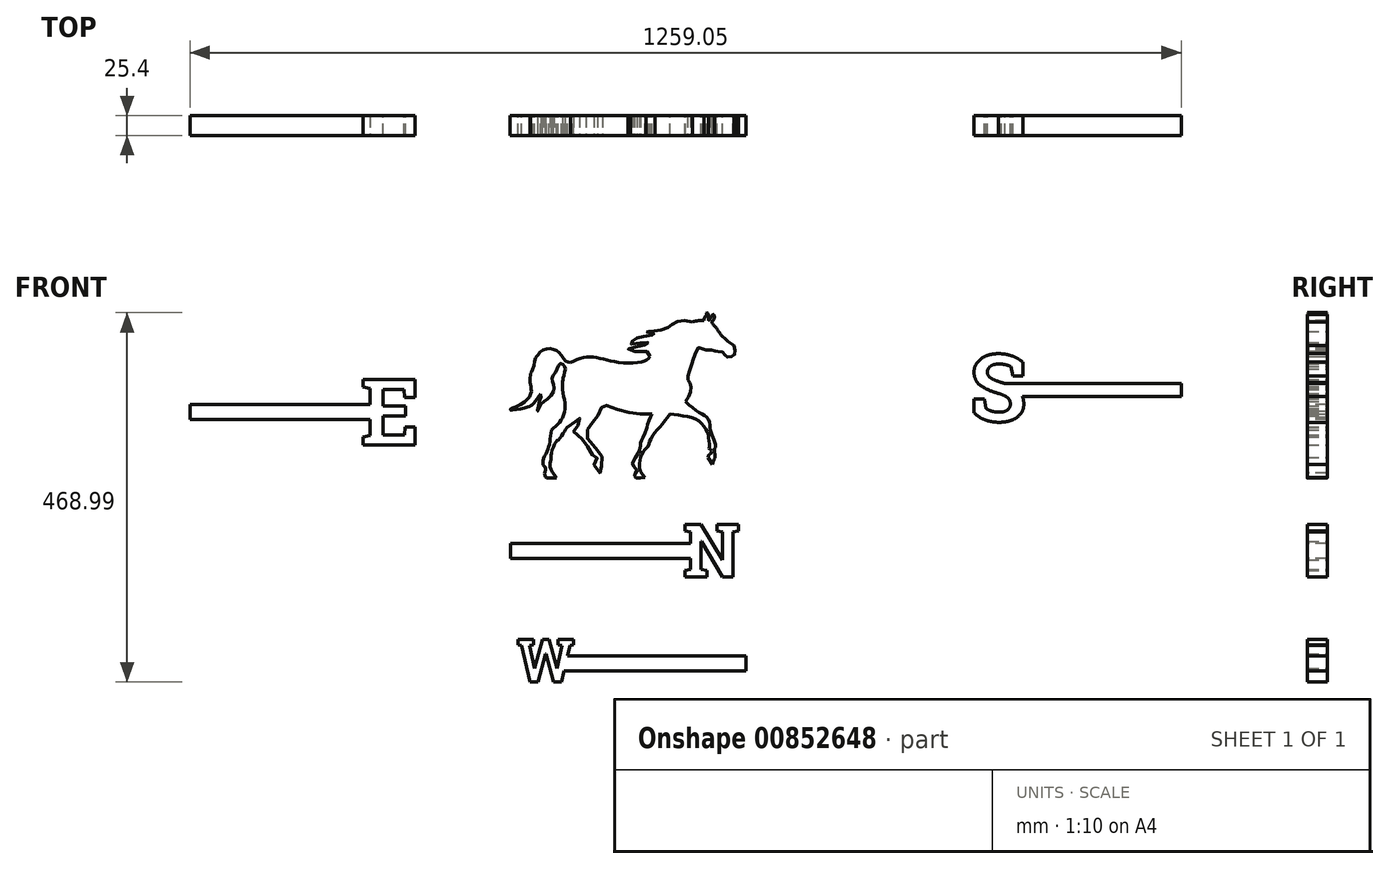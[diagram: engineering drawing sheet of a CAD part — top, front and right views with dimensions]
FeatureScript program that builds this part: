
annotation { "Feature Type Name" : "Feature", "Feature Type Description" : "" }
export const myFeature = defineFeature(function(context is Context, id is Id, definition is map)
    precondition{}
    {
        {
            var Q0;
            Q0=qCreatedBy(makeId("Front.planeOp"),FACE);
            var sketch = newSketch(context, id + "F0", { "sketchPlane" : qUnion([Q0])});
            skFitSpline(sketch, "E0", {"points": [v(155.5, 210.54) * mm, v(173.74, 216.9) * mm, v(192.53, 215.79) * mm, v(216.57, 210.54) * mm, v(248.62, 211.92) * mm, v(256.36, 217.72) * mm, v(273.76, 237.07) * mm, v(292.55, 252.27) * mm, v(310.24, 261.94) * mm, v(324.6, 263.88) * mm], "startDerivative": vector(167.31, 74.76) * mm, "endDerivative": vector(151.86, 5.73) * mm});
            skFitSpline(sketch, "E1", {"points": [v(324.6, 263.88) * mm, v(326.8, 269.35) * mm, v(327.97, 270.63) * mm, v(328.55, 273.53) * mm, v(330.64, 270.86) * mm, v(330.87, 263.88) * mm, v(336.68, 271.32) * mm, v(337.5, 265.17) * mm, v(334.7, 261.8) * mm, v(339.35, 255.52) * mm, v(347.49, 244.48) * mm, v(362.7, 232.05) * mm], "startDerivative": vector(24.18, 79.73) * mm, "endDerivative": vector(109.46, -77.63) * mm});
            skLineSegment(sketch, "E2", {"start": v(334.7, 261.8) * mm, "end": v(336.68, 271.32) * mm});
            skFitSpline(sketch, "E3", {"points": [v(362.7, 232.05) * mm, v(364.22, 221.36) * mm, v(359.57, 217.87) * mm, v(352.37, 218) * mm, v(349.23, 223.34) * mm, v(340.52, 224.38) * mm, v(336.91, 226) * mm, v(325.53, 226.7) * mm, v(318.2, 229.5) * mm, v(312.28, 217.18) * mm, v(306.02, 198.3) * mm, v(304.27, 188.92) * mm, v(307.59, 182.66) * mm, v(307.69, 172.9) * mm, v(301.34, 160.58) * mm], "startDerivative": vector(46.46, -160.08) * mm, "endDerivative": vector(-88.77, -140.52) * mm});
            skFitSpline(sketch, "E4", {"points": [v(301.34, 160.58) * mm, v(316.39, 148.52) * mm, v(324.98, 143.15) * mm, v(330.06, 138.75) * mm, v(332.6, 130.93) * mm, v(333.1, 123.31) * mm, v(339.54, 103.38) * mm, v(337.98, 100.45) * mm, v(339.05, 90.97) * mm, v(337.2, 86.87) * mm, v(335.53, 80.8) * mm], "startDerivative": vector(107.76, -91.14) * mm, "endDerivative": vector(-14.64, -79.86) * mm});
            skLineSegment(sketch, "E5", {"start": v(335.53, 80.8) * mm, "end": v(330.06, 89.4) * mm});
            skFitSpline(sketch, "E6", {"points": [v(330.06, 89.4) * mm, v(330.75, 92.92) * mm, v(333.58, 94.3) * mm, v(334.07, 99.67) * mm, v(331.33, 100.74) * mm, v(331.72, 104.36) * mm, v(330.94, 112.56) * mm, v(330.06, 120.67) * mm, v(324.88, 129.08) * mm, v(315.6, 137.77) * mm, v(298.8, 142.46) * mm, v(281.7, 144.9) * mm], "startDerivative": vector(-0.67, 69.7) * mm, "endDerivative": vector(-122.74, 16.45) * mm});
            skFitSpline(sketch, "E7", {"points": [v(281.7, 144.9) * mm, v(271.15, 130.93) * mm, v(260.4, 118.65) * mm, v(255.72, 109.08) * mm, v(253.57, 103.38) * mm, v(249.47, 99.67) * mm, v(244.97, 91.1) * mm, v(243.21, 82.5) * mm, v(243.07, 75.41) * mm, v(250.13, 64.4) * mm], "startDerivative": vector(-68.9, -98.06) * mm, "endDerivative": vector(72.71, -90.96) * mm});
            skFitSpline(sketch, "E8", {"points": [v(250.13, 64.4) * mm, v(237.69, 64.4) * mm, v(237.2, 69.26) * mm, v(239.54, 73.56) * mm, v(235.64, 78.54) * mm, v(234.27, 82.5) * mm, v(238.47, 90.95) * mm, v(243.94, 101.6) * mm, v(244.43, 109.32) * mm, v(246.87, 114.5) * mm, v(251.82, 126.23) * mm, v(252.23, 127.8) * mm, v(254.86, 136.42) * mm, v(258.72, 144.9) * mm], "startDerivative": vector(-155.51, -25.86) * mm, "endDerivative": vector(45.7, 89.67) * mm});
            skFitSpline(sketch, "E9", {"points": [v(258.72, 144.9) * mm, v(241.65, 144.9) * mm, v(223.83, 148.08) * mm, v(206.42, 153.75) * mm, v(196.33, 156.51) * mm, v(194.12, 150.3) * mm, v(189.43, 141.86) * mm, v(182.93, 133.85) * mm, v(177.27, 125.97) * mm, v(175.75, 115.75) * mm, v(188.73, 100.27) * mm, v(195.5, 89.08) * mm, v(194.68, 77.47) * mm, v(193.16, 70.01) * mm, v(185.28, 79.4) * mm, v(187.35, 84.1) * mm, v(189.01, 91.3) * mm, v(183.48, 92.81) * mm, v(177, 103.31) * mm, v(169.8, 113.12) * mm, v(159.17, 123.63) * mm, v(163.73, 129.43) * mm, v(166.77, 135.1) * mm, v(166.21, 140.62) * mm, v(162.48, 136.34) * mm, v(150.74, 128.05) * mm], "startDerivative": vector(-332.87, -13.48) * mm, "endDerivative": vector(-283.34, -157.92) * mm});
            skFitSpline(sketch, "E10", {"points": [v(150.74, 128.05) * mm, v(145.93, 120.3) * mm, v(139.98, 112.16) * mm, v(136.67, 109.53) * mm, v(131.42, 96.54) * mm, v(130.59, 88.53) * mm, v(129.48, 83.14) * mm, v(129.62, 76.92) * mm, v(137.36, 63.52) * mm], "startDerivative": vector(-35.37, -57.03) * mm, "endDerivative": vector(59.69, -86.9) * mm});
            skLineSegment(sketch, "E11", {"start": v(137.36, 63.52) * mm, "end": v(125.06, 63.52) * mm});
            skFitSpline(sketch, "E12", {"points": [v(125.06, 63.52) * mm, v(122.58, 67.8) * mm, v(123.27, 73.33) * mm, v(123, 77.61) * mm, v(120.78, 80.24) * mm, v(121.06, 87.84) * mm, v(126.03, 98.48) * mm, v(128.93, 109.4) * mm, v(131.28, 124.73) * mm], "startDerivative": vector(-32.82, 39.9) * mm, "endDerivative": vector(12.86, 89.42) * mm});
            skFitSpline(sketch, "E13", {"points": [v(131.28, 124.73) * mm, v(139.5, 132.14) * mm, v(145.95, 141.9) * mm, v(148.49, 155.59) * mm, v(145.75, 172.2) * mm, v(144.97, 185.88) * mm, v(145.75, 189.2) * mm, v(149.27, 201.9) * mm, v(155.5, 210.54) * mm], "startDerivative": vector(69.41, 57.06) * mm, "endDerivative": vector(57.1, 60.66) * mm});
            skFitSpline(sketch, "E14", {"points": [v(149.27, 201.9) * mm, v(146.66, 207.13) * mm, v(142.12, 209) * mm, v(137.72, 200.47) * mm, v(132.52, 192.2) * mm, v(132.52, 185.26) * mm, v(134.52, 176.46) * mm, v(125.72, 163.65) * mm, v(116.65, 155.52) * mm, v(113.31, 148.05) * mm, v(116.11, 161.65) * mm, v(116.91, 170.06) * mm, v(104.91, 180.06) * mm, v(104.38, 194.2) * mm, v(104.38, 196.46) * mm, v(107.45, 201.9) * mm, v(110.91, 216.07) * mm, v(113.18, 219) * mm, v(120.38, 226.34) * mm, v(132.92, 227.27) * mm, v(141.19, 222.47) * mm, v(149.27, 212.07) * mm, v(155.5, 210.54) * mm], "startDerivative": vector(-73.14, 221) * mm, "endDerivative": vector(242.16, -2.9) * mm});
            skFitSpline(sketch, "E15.trimOffspring", {"points": [v(149.27, 201.9) * mm, v(146.66, 207.13) * mm, v(142.12, 209) * mm, v(137.72, 200.47) * mm, v(132.52, 192.2) * mm, v(132.52, 185.26) * mm, v(134.52, 176.46) * mm, v(125.72, 163.65) * mm, v(116.65, 155.52) * mm, v(113.31, 148.05) * mm, v(116.11, 161.65) * mm, v(116.91, 170.06) * mm, v(104.91, 180.06) * mm, v(104.38, 194.2) * mm, v(104.38, 196.46) * mm, v(107.45, 201.9) * mm, v(110.91, 216.07) * mm, v(113.18, 219) * mm, v(120.38, 226.34) * mm, v(132.92, 227.27) * mm, v(141.19, 222.47) * mm, v(149.27, 212.07) * mm, v(155.5, 210.54) * mm], "startDerivative": vector(-73.14, 221) * mm, "endDerivative": vector(242.16, -2.9) * mm});
            skFitSpline(sketch, "E16", {"points": [v(104.91, 180.06) * mm, v(104.91, 170.72) * mm, v(91.78, 156.72) * mm, v(78.45, 150.31) * mm, v(94.05, 151.65) * mm, v(104.91, 155.38) * mm, v(106.86, 156.72) * mm, v(116.91, 170.06) * mm], "startDerivative": vector(12.52, -71.7) * mm, "endDerivative": vector(72.4, 101.25) * mm});
            skFitSpline(sketch, "E17", {"points": [v(310.24, 261.94) * mm, v(296.7, 263.59) * mm, v(286.52, 260.38) * mm, v(282, 256.8) * mm, v(274.26, 252.84) * mm, v(261.81, 250.2) * mm, v(257.85, 249.82) * mm, v(251.44, 249.82) * mm, v(256.53, 247.74) * mm, v(262.56, 246.42) * mm, v(252.2, 244.16) * mm, v(240.68, 241.9) * mm, v(234.84, 238.31) * mm, v(231.44, 234.16) * mm, v(244.08, 235.1) * mm, v(253.89, 235.67) * mm, v(242, 230.58) * mm, v(228.61, 227.75) * mm, v(237.67, 224.16) * mm, v(240.68, 224.16) * mm, v(252.38, 224.35) * mm, v(256.36, 217.72) * mm], "startDerivative": vector(-229.47, 50.05) * mm, "endDerivative": vector(46.47, -183.94) * mm});
            skSolve(sketch);
        }
        {
            var Q0;
            Q0 = qSketchRegion(id + "F0", true);
            extrude(context, id + "F1", {"entities" : qUnion([Q0]), "depth" : 25.4 * mm, "offsetDistance" : 25.4 * mm});
        }
        {
            var Q0;
            Q0 = qSketchRegion(id + "F0", true);
            extrude(context, id + "F2", {"entities" : qUnion([Q0]), "operationType" : NewBodyOperationType.ADD, "depth" : 25.4 * mm, "offsetDistance" : 25.4 * mm});
        }
        {
            var Q0;
            Q0=qCreatedBy(makeId("Front.planeOp"),FACE);
            var sketch = newSketch(context, id + "F3", { "sketchPlane" : qUnion([Q0])});
            skText(sketch, "E18", { "text": "N", "fontName": "RobotoSlab-Bold.ttf"});
            const initialGuessF3  = {"E18": [0.29832, -0.06195, 1, 0, 0.0673]};
            skSetInitialGuess(sketch, initialGuessF3);
            skSolve(sketch);
        }
        {
            var Q0;
            Q0 = qSketchRegion(id + "F3", true);
            extrude(context, id + "F4", {"entities" : qUnion([Q0]), "depth" : 25.4 * mm, "offsetDistance" : 25.4 * mm});
        }
        {
            var Q0;
            Q0=makeQuery(id+"F4.opExtrude","CAP_FACE",FACE,{"disambiguationData":[OSD([sQuery(id+"F3.wireOp",EDGE,"E18.sketch_text.stroke-0"),sQuery(id+"F3.wireOp",EDGE,"E18.sketch_text.stroke-1"),sQuery(id+"F3.wireOp",EDGE,"E18.sketch_text.stroke-2"),sQuery(id+"F3.wireOp",EDGE,"E18.sketch_text.stroke-3"),sQuery(id+"F3.wireOp",EDGE,"E18.sketch_text.stroke-4"),sQuery(id+"F3.wireOp",EDGE,"E18.sketch_text.stroke-5"),sQuery(id+"F3.wireOp",EDGE,"E18.sketch_text.stroke-6"),sQuery(id+"F3.wireOp",EDGE,"E18.sketch_text.stroke-7"),sQuery(id+"F3.wireOp",EDGE,"E18.sketch_text.stroke-8"),sQuery(id+"F3.wireOp",EDGE,"E18.sketch_text.stroke-9"),sQuery(id+"F3.wireOp",EDGE,"E18.sketch_text.stroke-10"),sQuery(id+"F3.wireOp",EDGE,"E18.sketch_text.stroke-11"),sQuery(id+"F3.wireOp",EDGE,"E18.sketch_text.stroke-12"),sQuery(id+"F3.wireOp",EDGE,"E18.sketch_text.stroke-13"),sQuery(id+"F3.wireOp",EDGE,"E18.sketch_text.stroke-14"),sQuery(id+"F3.wireOp",EDGE,"E18.sketch_text.stroke-15"),sQuery(id+"F3.wireOp",EDGE,"E18.sketch_text.stroke-16"),sQuery(id+"F3.wireOp",EDGE,"E18.sketch_text.stroke-17"),sQuery(id+"F3.wireOp",EDGE,"E18.sketch_text.stroke-18"),sQuery(id+"F3.wireOp",EDGE,"E18.sketch_text.stroke-19"),sQuery(id+"F3.wireOp",EDGE,"E18.sketch_text.stroke-20"),sQuery(id+"F3.wireOp",EDGE,"E18.sketch_text.stroke-21"),sQuery(id+"F3.wireOp",EDGE,"E18.sketch_text.stroke-22"),sQuery(id+"F3.wireOp",EDGE,"E18.sketch_text.stroke-23")])],"isStart":false});
            var sketch = newSketch(context, id + "F5", { "sketchPlane" : qUnion([Q0])});
            skLineSegment(sketch, "E19.0", {"start": v(307.95, -19.22) * mm, "end": v(79.35, -19.22) * mm});
            skLineSegment(sketch, "E20.0", {"start": v(307.95, -38.27) * mm, "end": v(79.35, -38.27) * mm});
            skLineSegment(sketch, "E21", {"start": v(79.35, -19.22) * mm, "end": v(79.35, -38.27) * mm});
            skSolve(sketch);
        }
        {
            var Q0;
            Q0 = qSketchRegion(id + "F5", true);
            var Q1;
            {var subQ0=sQuery(id+"F5.wireOp",EDGE,"E19.0");Q1=makeQuery(id+"F5.imprint","IMPRINT",FACE,{"disambiguationData":[TD([[makeQuery(id+"F5.imprint","IMPRINT",EDGE,{"derivedFrom":subQ0}),1.0]])]});}
            extrude(context, id + "F6", {"entities" : qUnion([Q0, Q1]), "operationType" : NewBodyOperationType.ADD, "oppositeDirection" : true, "depth" : 25.4 * mm, "offsetDistance" : 25.4 * mm});
        }
        {
            var Q0;
            Q0=qCreatedBy(makeId("Front.planeOp"),FACE);
            var sketch = newSketch(context, id + "F7", { "sketchPlane" : qUnion([Q0])});
            skText(sketch, "E22", { "text": "S", "fontName": "RobotoSlab-Bold.ttf"});
            const initialGuessF7  = {"E22": [0.66224, 0.13563, 1, 0, 0.08587]};
            skSetInitialGuess(sketch, initialGuessF7);
            skSolve(sketch);
        }
        {
            var Q0;
            Q0 = qSketchRegion(id + "F7", true);
            extrude(context, id + "F8", {"entities" : qUnion([Q0]), "depth" : 25.4 * mm, "offsetDistance" : 25.4 * mm});
        }
        {
            var Q0;
            Q0=makeQuery(id+"F8.opExtrude","CAP_FACE",FACE,{"disambiguationData":[OSD([sQuery(id+"F7.wireOp",EDGE,"E22.sketch_text.stroke-0"),sQuery(id+"F7.wireOp",EDGE,"E22.sketch_text.stroke-1"),sQuery(id+"F7.wireOp",EDGE,"E22.sketch_text.stroke-2"),sQuery(id+"F7.wireOp",EDGE,"E22.sketch_text.stroke-3"),sQuery(id+"F7.wireOp",EDGE,"E22.sketch_text.stroke-4"),sQuery(id+"F7.wireOp",EDGE,"E22.sketch_text.stroke-5"),sQuery(id+"F7.wireOp",EDGE,"E22.sketch_text.stroke-6"),sQuery(id+"F7.wireOp",EDGE,"E22.sketch_text.stroke-7"),sQuery(id+"F7.wireOp",EDGE,"E22.sketch_text.stroke-8"),sQuery(id+"F7.wireOp",EDGE,"E22.sketch_text.stroke-9"),sQuery(id+"F7.wireOp",EDGE,"E22.sketch_text.stroke-10"),sQuery(id+"F7.wireOp",EDGE,"E22.sketch_text.stroke-11"),sQuery(id+"F7.wireOp",EDGE,"E22.sketch_text.stroke-12"),sQuery(id+"F7.wireOp",EDGE,"E22.sketch_text.stroke-13"),sQuery(id+"F7.wireOp",EDGE,"E22.sketch_text.stroke-14"),sQuery(id+"F7.wireOp",EDGE,"E22.sketch_text.stroke-15"),sQuery(id+"F7.wireOp",EDGE,"E22.sketch_text.stroke-16"),sQuery(id+"F7.wireOp",EDGE,"E22.sketch_text.stroke-17"),sQuery(id+"F7.wireOp",EDGE,"E22.sketch_text.stroke-18"),sQuery(id+"F7.wireOp",EDGE,"E22.sketch_text.stroke-19"),sQuery(id+"F7.wireOp",EDGE,"E22.sketch_text.stroke-20"),sQuery(id+"F7.wireOp",EDGE,"E22.sketch_text.stroke-21"),sQuery(id+"F7.wireOp",EDGE,"E22.sketch_text.stroke-22"),sQuery(id+"F7.wireOp",EDGE,"E22.sketch_text.stroke-23"),sQuery(id+"F7.wireOp",EDGE,"E22.sketch_text.stroke-24"),sQuery(id+"F7.wireOp",EDGE,"E22.sketch_text.stroke-25"),sQuery(id+"F7.wireOp",EDGE,"E22.sketch_text.stroke-26"),sQuery(id+"F7.wireOp",EDGE,"E22.sketch_text.stroke-27"),sQuery(id+"F7.wireOp",EDGE,"E22.sketch_text.stroke-28"),sQuery(id+"F7.wireOp",EDGE,"E22.sketch_text.stroke-29")])],"isStart":false});
            var sketch = newSketch(context, id + "F9", { "sketchPlane" : qUnion([Q0])});
            skLineSegment(sketch, "E23.0", {"start": v(721.45, 167.14) * mm, "end": v(931.2, 167.14) * mm});
            skLineSegment(sketch, "E24.0", {"start": v(694.4, 183.68) * mm, "end": v(931.2, 183.68) * mm});
            skLineSegment(sketch, "E25", {"start": v(931.2, 183.68) * mm, "end": v(931.2, 167.14) * mm});
            skLineSegment(sketch, "E26", {"start": v(694.4, 183.68) * mm, "end": v(721.45, 167.14) * mm});
            skSolve(sketch);
        }
        {
            var Q0;
            {var subQ1=sQuery(id+"F9.wireOp",EDGE,"E26");Q0=makeQuery(id+"F9.imprint","IMPRINT",FACE,{"disambiguationData":[TD([[makeQuery(id+"F9.imprint","IMPRINT",EDGE,{"derivedFrom":subQ1}),1.0]])]});}
            var Q1;
            {var subQ1=sQuery(id+"F9.wireOp",EDGE,"E25");Q1=makeQuery(id+"F9.imprint","IMPRINT",FACE,{"disambiguationData":[TD([[makeQuery(id+"F9.imprint","IMPRINT",EDGE,{"derivedFrom":subQ1}),-1.0]])]});}
            extrude(context, id + "F10", {"entities" : qUnion([Q0, Q1]), "operationType" : NewBodyOperationType.ADD, "oppositeDirection" : true, "depth" : 25.4 * mm, "offsetDistance" : 25.4 * mm});
        }
        {
            var Q0;
            Q0=qCreatedBy(makeId("Front.planeOp"),FACE);
            var sketch = newSketch(context, id + "F11", { "sketchPlane" : qUnion([Q0])});
            skText(sketch, "E27", { "text": "E", "fontName": "RobotoSlab-Bold.ttf"});
            const initialGuessF11  = {"E27": [-0.1113, 0.10581, 1, 0, 0.08426]};
            skSetInitialGuess(sketch, initialGuessF11);
            skSolve(sketch);
        }
        {
            var Q0;
            Q0 = qSketchRegion(id + "F11", true);
            extrude(context, id + "F12", {"entities" : qUnion([Q0]), "depth" : 25.4 * mm, "offsetDistance" : 25.4 * mm});
        }
        {
            var Q0;
            Q0=makeQuery(id+"F12.opExtrude","CAP_FACE",FACE,{"disambiguationData":[OSD([sQuery(id+"F11.wireOp",EDGE,"E27.sketch_text.stroke-0"),sQuery(id+"F11.wireOp",EDGE,"E27.sketch_text.stroke-1"),sQuery(id+"F11.wireOp",EDGE,"E27.sketch_text.stroke-2"),sQuery(id+"F11.wireOp",EDGE,"E27.sketch_text.stroke-3"),sQuery(id+"F11.wireOp",EDGE,"E27.sketch_text.stroke-4"),sQuery(id+"F11.wireOp",EDGE,"E27.sketch_text.stroke-5"),sQuery(id+"F11.wireOp",EDGE,"E27.sketch_text.stroke-6"),sQuery(id+"F11.wireOp",EDGE,"E27.sketch_text.stroke-7"),sQuery(id+"F11.wireOp",EDGE,"E27.sketch_text.stroke-8"),sQuery(id+"F11.wireOp",EDGE,"E27.sketch_text.stroke-9"),sQuery(id+"F11.wireOp",EDGE,"E27.sketch_text.stroke-10"),sQuery(id+"F11.wireOp",EDGE,"E27.sketch_text.stroke-11"),sQuery(id+"F11.wireOp",EDGE,"E27.sketch_text.stroke-12"),sQuery(id+"F11.wireOp",EDGE,"E27.sketch_text.stroke-13"),sQuery(id+"F11.wireOp",EDGE,"E27.sketch_text.stroke-14"),sQuery(id+"F11.wireOp",EDGE,"E27.sketch_text.stroke-15"),sQuery(id+"F11.wireOp",EDGE,"E27.sketch_text.stroke-16"),sQuery(id+"F11.wireOp",EDGE,"E27.sketch_text.stroke-17"),sQuery(id+"F11.wireOp",EDGE,"E27.sketch_text.stroke-18"),sQuery(id+"F11.wireOp",EDGE,"E27.sketch_text.stroke-19"),sQuery(id+"F11.wireOp",EDGE,"E27.sketch_text.stroke-20")])],"isStart":false});
            var sketch = newSketch(context, id + "F13", { "sketchPlane" : qUnion([Q0])});
            skLineSegment(sketch, "E28.0", {"start": v(-99.25, 156.91) * mm, "end": v(-327.85, 156.91) * mm});
            skLineSegment(sketch, "E29.0", {"start": v(-99.25, 137.86) * mm, "end": v(-327.85, 137.86) * mm});
            skLineSegment(sketch, "E30", {"start": v(-327.85, 156.91) * mm, "end": v(-327.85, 137.86) * mm});
            skSolve(sketch);
        }
        {
            var Q0;
            Q0 = qSketchRegion(id + "F13", true);
            var Q1;
            {var subQ0=sQuery(id+"F13.wireOp",EDGE,"E28.0");Q1=makeQuery(id+"F13.imprint","IMPRINT",FACE,{"disambiguationData":[TD([[makeQuery(id+"F13.imprint","IMPRINT",EDGE,{"derivedFrom":subQ0}),1.0]])]});}
            extrude(context, id + "F14", {"entities" : qUnion([Q0, Q1]), "operationType" : NewBodyOperationType.ADD, "oppositeDirection" : true, "depth" : 25.4 * mm, "offsetDistance" : 25.4 * mm});
        }
        {
            var Q0;
            Q0=qCreatedBy(makeId("Front.planeOp"),FACE);
            var sketch = newSketch(context, id + "F15", { "sketchPlane" : qUnion([Q0])});
            skText(sketch, "E31", { "text": "W", "fontName": "RobotoSlab-Bold.ttf"});
            const initialGuessF15  = {"E31": [0.08757, -0.19538, 1, 0, 0.05435]};
            skSetInitialGuess(sketch, initialGuessF15);
            skSolve(sketch);
        }
        {
            var Q0;
            Q0 = qSketchRegion(id + "F15", true);
            extrude(context, id + "F16", {"entities" : qUnion([Q0]), "depth" : 25.4 * mm, "offsetDistance" : 25.4 * mm});
        }
        {
            var Q0;
            Q0=makeQuery(id+"F16.opExtrude","CAP_FACE",FACE,{"disambiguationData":[OSD([sQuery(id+"F15.wireOp",EDGE,"E31.sketch_text.stroke-0"),sQuery(id+"F15.wireOp",EDGE,"E31.sketch_text.stroke-1"),sQuery(id+"F15.wireOp",EDGE,"E31.sketch_text.stroke-2"),sQuery(id+"F15.wireOp",EDGE,"E31.sketch_text.stroke-3"),sQuery(id+"F15.wireOp",EDGE,"E31.sketch_text.stroke-4"),sQuery(id+"F15.wireOp",EDGE,"E31.sketch_text.stroke-5"),sQuery(id+"F15.wireOp",EDGE,"E31.sketch_text.stroke-6"),sQuery(id+"F15.wireOp",EDGE,"E31.sketch_text.stroke-7"),sQuery(id+"F15.wireOp",EDGE,"E31.sketch_text.stroke-8"),sQuery(id+"F15.wireOp",EDGE,"E31.sketch_text.stroke-9"),sQuery(id+"F15.wireOp",EDGE,"E31.sketch_text.stroke-10"),sQuery(id+"F15.wireOp",EDGE,"E31.sketch_text.stroke-11"),sQuery(id+"F15.wireOp",EDGE,"E31.sketch_text.stroke-12"),sQuery(id+"F15.wireOp",EDGE,"E31.sketch_text.stroke-13"),sQuery(id+"F15.wireOp",EDGE,"E31.sketch_text.stroke-14"),sQuery(id+"F15.wireOp",EDGE,"E31.sketch_text.stroke-15"),sQuery(id+"F15.wireOp",EDGE,"E31.sketch_text.stroke-16"),sQuery(id+"F15.wireOp",EDGE,"E31.sketch_text.stroke-17"),sQuery(id+"F15.wireOp",EDGE,"E31.sketch_text.stroke-18"),sQuery(id+"F15.wireOp",EDGE,"E31.sketch_text.stroke-19"),sQuery(id+"F15.wireOp",EDGE,"E31.sketch_text.stroke-20"),sQuery(id+"F15.wireOp",EDGE,"E31.sketch_text.stroke-21"),sQuery(id+"F15.wireOp",EDGE,"E31.sketch_text.stroke-22"),sQuery(id+"F15.wireOp",EDGE,"E31.sketch_text.stroke-23")])],"isStart":false});
            var sketch = newSketch(context, id + "F17", { "sketchPlane" : qUnion([Q0])});
            skLineSegment(sketch, "E32.0", {"start": v(149.3, -162.54) * mm, "end": v(377.9, -162.54) * mm});
            skLineSegment(sketch, "E33.0", {"start": v(141.2, -181.6) * mm, "end": v(377.9, -181.6) * mm});
            skLineSegment(sketch, "E34", {"start": v(377.9, -162.54) * mm, "end": v(377.9, -181.6) * mm});
            skLineSegment(sketch, "E35", {"start": v(149.3, -162.54) * mm, "end": v(141.2, -181.6) * mm});
            skSolve(sketch);
        }
        {
            var Q0;
            {var subQ0=sQuery(id+"F17.wireOp",EDGE,"E35");Q0=makeQuery(id+"F17.imprint","IMPRINT",FACE,{"disambiguationData":[TD([[makeQuery(id+"F17.imprint","IMPRINT",EDGE,{"derivedFrom":subQ0}),1.0]])]});}
            var Q1;
            {var subQ0=sQuery(id+"F17.wireOp",EDGE,"E34");Q1=makeQuery(id+"F17.imprint","IMPRINT",FACE,{"disambiguationData":[TD([[makeQuery(id+"F17.imprint","IMPRINT",EDGE,{"derivedFrom":subQ0}),-1.0]])]});}
            extrude(context, id + "F18", {"entities" : qUnion([Q0, Q1]), "operationType" : NewBodyOperationType.ADD, "oppositeDirection" : true, "depth" : 25.4 * mm, "offsetDistance" : 25.4 * mm});
        }
    });
